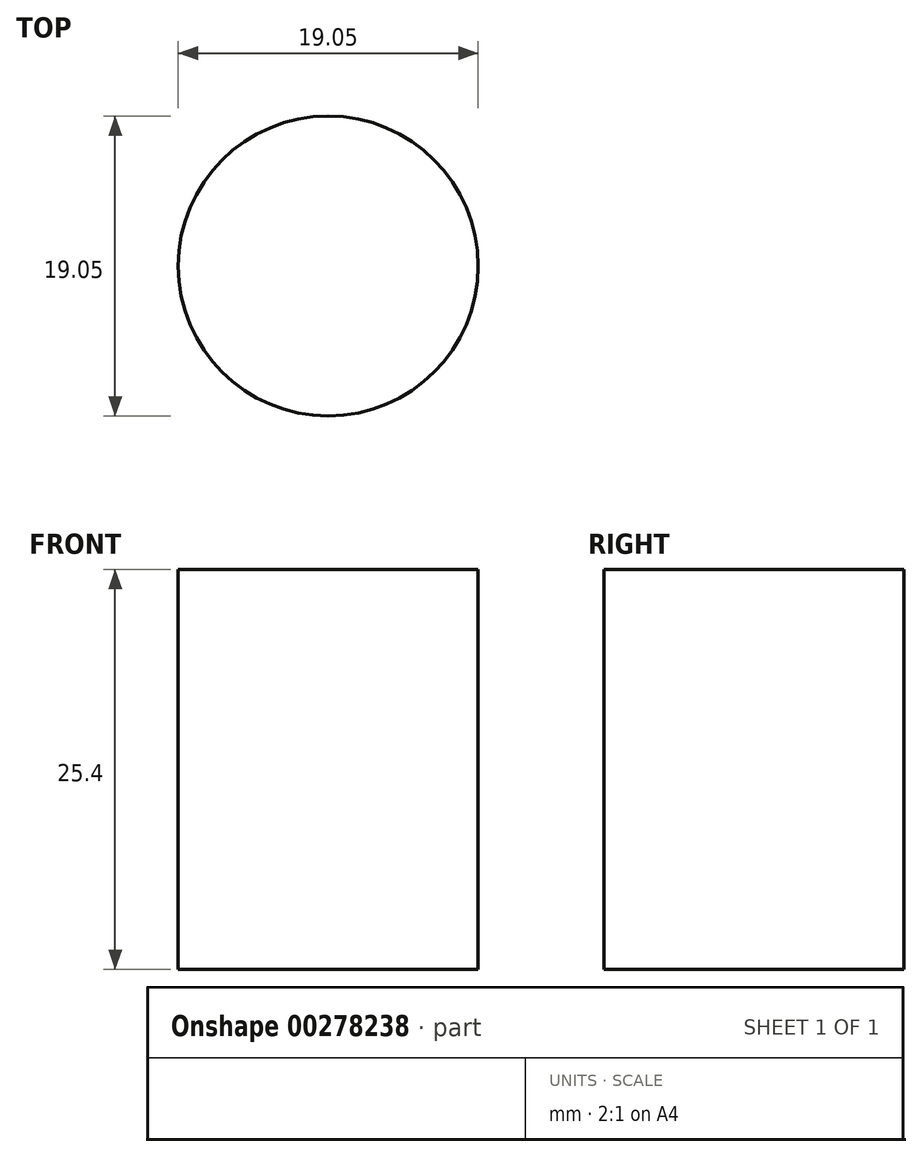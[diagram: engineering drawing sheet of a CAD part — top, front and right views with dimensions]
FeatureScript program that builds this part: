
annotation { "Feature Type Name" : "Feature", "Feature Type Description" : "" }
export const myFeature = defineFeature(function(context is Context, id is Id, definition is map)
    precondition{}
    {
        {
            var Q0;
            Q0=qCreatedBy(makeId("Top.planeOp"),FACE);
            var sketch = newSketch(context, id + "F0", { "sketchPlane" : qUnion([Q0])});
            skCircle(sketch, "E0", {"center": v(-50.31, -37.81) * mm, "radius": 9.53 * mm});
            skSolve(sketch);
        }
        {
            var Q0;
            Q0=qSketchRegion(id+"F0",true);
            extrude(context, id + "F1", {"entities" : qUnion([Q0]), "depth" : 25.4 * mm});
        }
    });
